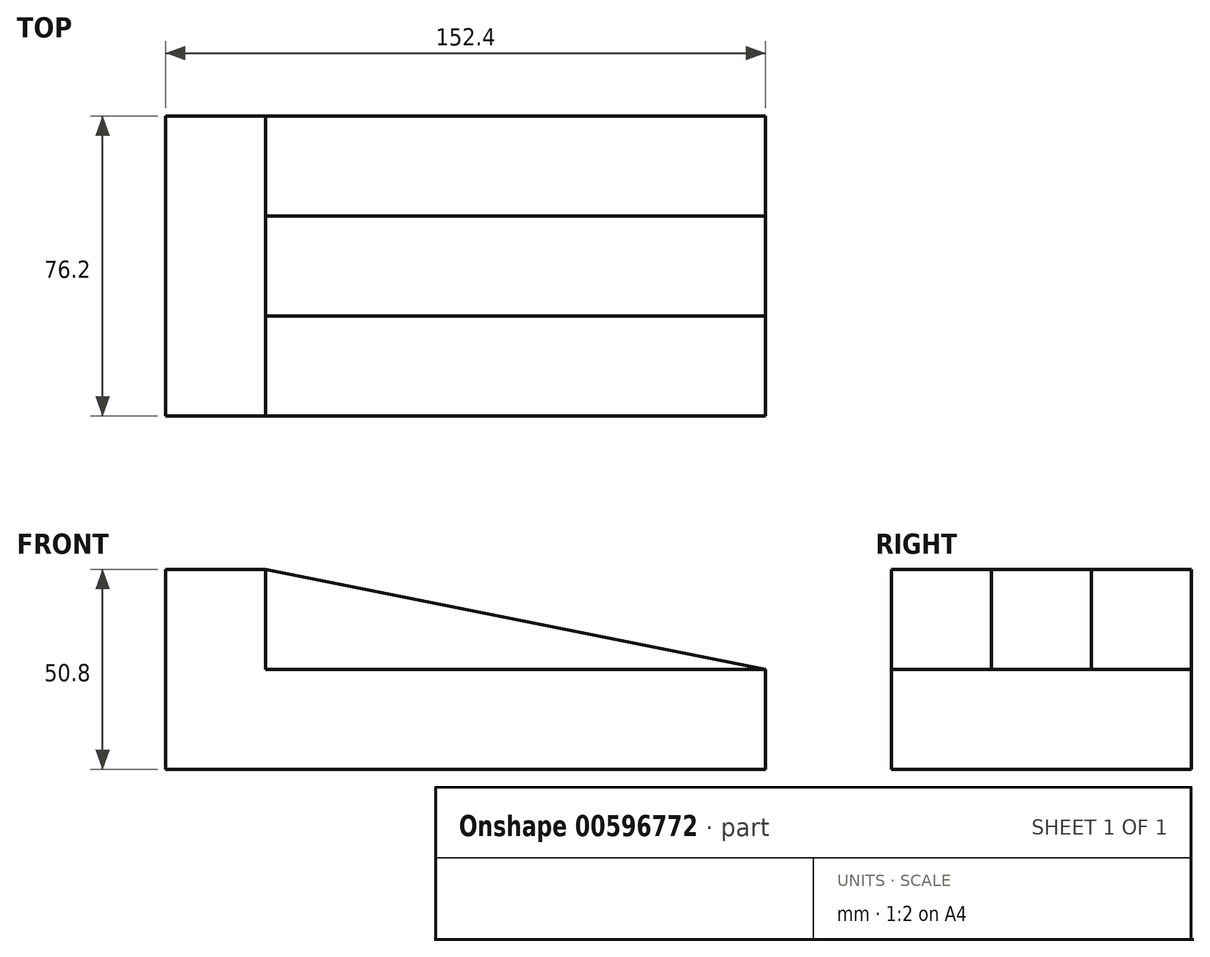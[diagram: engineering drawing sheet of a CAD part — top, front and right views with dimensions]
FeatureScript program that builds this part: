
annotation { "Feature Type Name" : "Feature", "Feature Type Description" : "" }
export const myFeature = defineFeature(function(context is Context, id is Id, definition is map)
    precondition{}
    {
        {
            var Q0;
            Q0=qCreatedBy(makeId("Front.planeOp"),FACE);
            var sketch = newSketch(context, id + "F0", { "sketchPlane" : qUnion([Q0])});
            skLineSegment(sketch, "E0", {"start": v(-76.7, -75.82) * mm, "end": v(75.7, -75.82) * mm});
            skLineSegment(sketch, "E1", {"start": v(75.7, -75.82) * mm, "end": v(75.7, -50.42) * mm});
            skLineSegment(sketch, "E2", {"start": v(75.7, -50.42) * mm, "end": v(-76.7, -50.42) * mm});
            skLineSegment(sketch, "E3", {"start": v(-76.7, -50.42) * mm, "end": v(-76.7, -75.82) * mm});
            skSolve(sketch);
        }
        {
            var Q0;
            Q0=makeQuery(id+"F0.imprint","IMPRINT",FACE,{"disambiguationData":[TD([[makeQuery(id+"F0.imprint","IMPRINT",EDGE,{"derivedFrom":sQuery(id+"F0.wireOp",EDGE,"E0")}),1.0]])]});
            extrude(context, id + "F1", {"entities" : qUnion([Q0]), "depth" : 76.2 * mm, "offsetDistance" : 25.4 * mm});
        }
        {
            var Q0;
            Q0=makeQuery(id+"F1.opExtrude","SWEPT_FACE",FACE,{"disambiguationData":[OSD([sQuery(id+"F0.wireOp",EDGE,"E2")])]});
            var sketch = newSketch(context, id + "F2", { "sketchPlane" : qUnion([Q0])});
            skLineSegment(sketch, "E4", {"start": v(-76.7, 0) * mm, "end": v(-51.3, 0) * mm});
            skLineSegment(sketch, "E5", {"start": v(-51.3, 0) * mm, "end": v(-51.3, -76.2) * mm});
            skLineSegment(sketch, "E6", {"start": v(-51.3, -76.2) * mm, "end": v(-76.7, -76.2) * mm});
            skLineSegment(sketch, "E7", {"start": v(-76.7, -76.2) * mm, "end": v(-76.7, 0) * mm});
            skSolve(sketch);
        }
        {
            var Q0;
            Q0=makeQuery(id+"F2.imprint","IMPRINT",FACE,{"disambiguationData":[TD([[makeQuery(id+"F2.imprint","IMPRINT",EDGE,{"derivedFrom":sQuery(id+"F2.wireOp",EDGE,"E4")}),1.0]])]});
            extrude(context, id + "F3", {"entities" : qUnion([Q0]), "operationType" : NewBodyOperationType.ADD, "depth" : 25.4 * mm, "offsetDistance" : 25.4 * mm});
        }
        {
            var Q0;
            Q0=makeQuery(id+"F1.opExtrude","SWEPT_FACE",FACE,{"disambiguationData":[OSD([sQuery(id+"F0.wireOp",EDGE,"E2")])]});
            var sketch = newSketch(context, id + "F4", { "sketchPlane" : qUnion([Q0])});
            skLineSegment(sketch, "E8", {"start": v(-51.3, 0) * mm, "end": v(-51.3, -25.4) * mm});
            skLineSegment(sketch, "E9", {"start": v(-51.3, -25.4) * mm, "end": v(75.7, -25.4) * mm});
            skLineSegment(sketch, "E10", {"start": v(75.7, -25.4) * mm, "end": v(75.7, -50.8) * mm});
            skLineSegment(sketch, "E11", {"start": v(75.7, -50.8) * mm, "end": v(-51.3, -50.8) * mm});
            skSolve(sketch);
        }
        {
            var Q0;
            {var subQ0=sQuery(id+"F4.wireOp",EDGE,"E9");Q0=makeQuery(id+"F4.imprint","IMPRINT",FACE,{"disambiguationData":[TD([[makeQuery(id+"F4.imprint","IMPRINT",EDGE,{"derivedFrom":subQ0}),-1.0]])]});}
            extrude(context, id + "F5", {"entities" : qUnion([Q0]), "operationType" : NewBodyOperationType.ADD, "depth" : 25.4 * mm, "offsetDistance" : 25.4 * mm});
        }
        {
            var Q0;
            Q0=makeQuery(id+"F5.opExtrude","SWEPT_FACE",FACE,{"disambiguationData":[OSD([sQuery(id+"F4.wireOp",EDGE,"E11")])]});
            var sketch = newSketch(context, id + "F6", { "sketchPlane" : qUnion([Q0])});
            skLineSegment(sketch, "E12", {"start": v(-51.3, -25.02) * mm, "end": v(75.7, -50.42) * mm});
            skSolve(sketch);
        }
        {
            var Q0;
            Q0=makeQuery(id+"F6.imprint","IMPRINT",FACE,{"disambiguationData":[TD([[makeQuery(id+"F6.imprint","IMPRINT",EDGE,{"derivedFrom":sQuery(id+"F6.wireOp",EDGE,"E12")}),1.0]])]});
            extrude(context, id + "F7", {"entities" : qUnion([Q0]), "operationType" : NewBodyOperationType.REMOVE, "oppositeDirection" : true, "depth" : 25.4 * mm, "offsetDistance" : 25.4 * mm});
        }
    });
